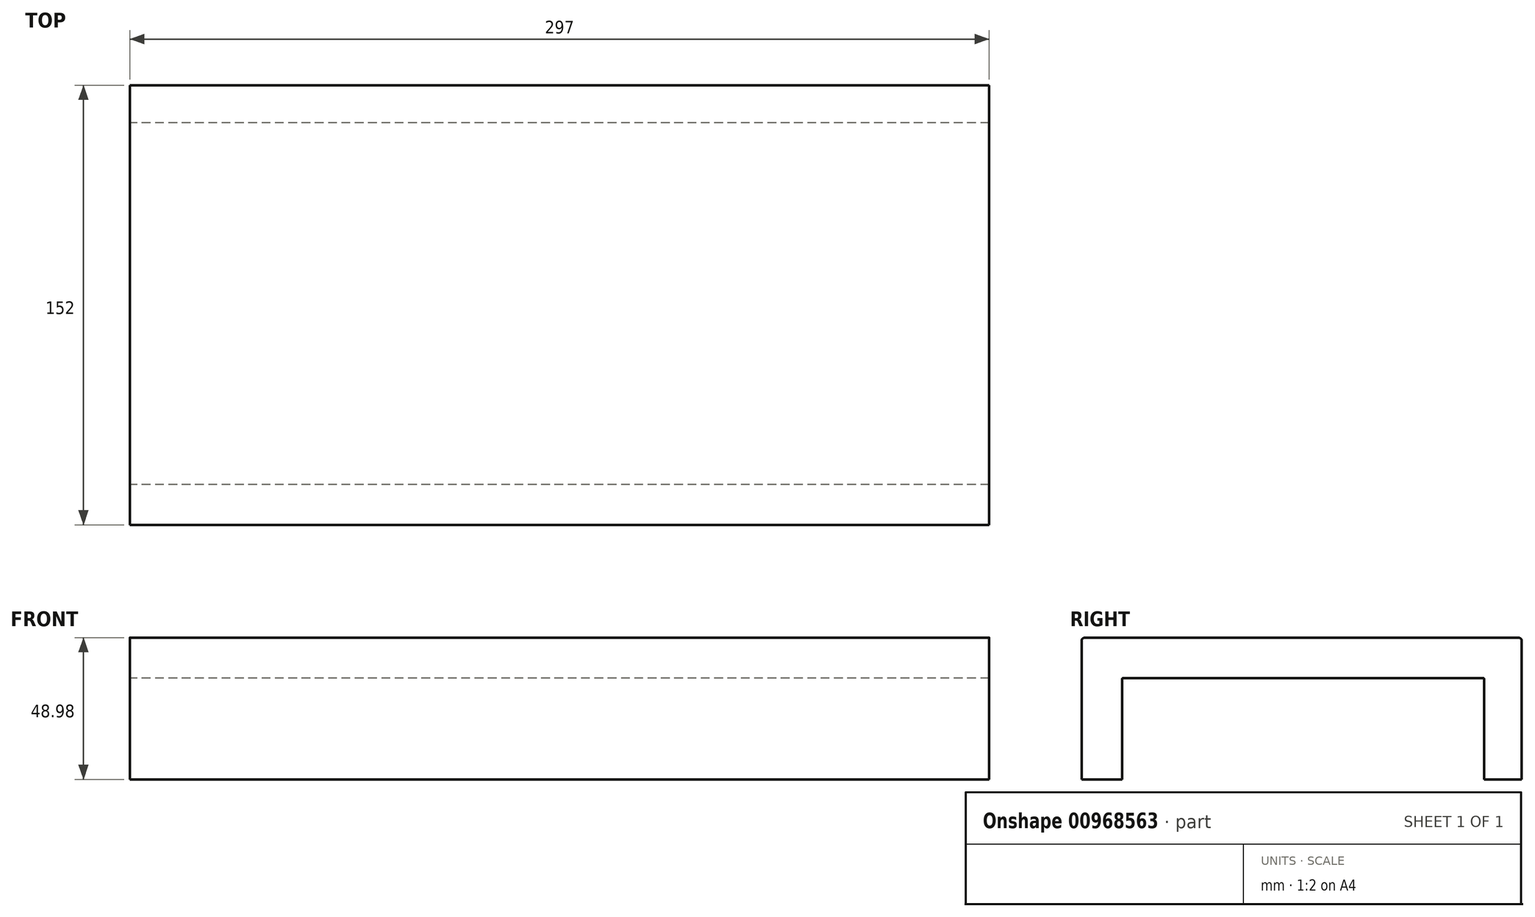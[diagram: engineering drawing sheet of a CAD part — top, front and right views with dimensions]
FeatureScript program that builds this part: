
annotation { "Feature Type Name" : "Feature", "Feature Type Description" : "" }
export const myFeature = defineFeature(function(context is Context, id is Id, definition is map)
    precondition{}
    {
        {
            var Q0;
            Q0=qCreatedBy(makeId("Right.planeOp"),FACE);
            var sketch = newSketch(context, id + "F0", { "sketchPlane" : qUnion([Q0])});
            skLineSegment(sketch, "E0", {"start": v(-48.76, 0) * mm, "end": v(-48.76, 47.98) * mm});
            skLineSegment(sketch, "E1", {"start": v(-47.76, 48.98) * mm, "end": v(102.24, 48.98) * mm});
            skLineSegment(sketch, "E2", {"start": v(103.24, 47.98) * mm, "end": v(103.24, 0) * mm});
            skLineSegment(sketch, "E3", {"start": v(103.24, 0) * mm, "end": v(90.24, 0) * mm});
            skLineSegment(sketch, "E4", {"start": v(90.24, 0) * mm, "end": v(90.24, 34.78) * mm});
            skLineSegment(sketch, "E5", {"start": v(90.04, 34.98) * mm, "end": v(-34.56, 34.98) * mm});
            skLineSegment(sketch, "E6", {"start": v(-34.76, 34.78) * mm, "end": v(-34.76, 0) * mm});
            skLineSegment(sketch, "E7", {"start": v(-34.76, 0) * mm, "end": v(-48.76, 0) * mm});
            skArc(sketch, "E8.filletArc", {"start": v(-47.76, 48.98) * mm, "mid": v(-48.47, 48.7) * mm, "end": v(-48.76, 47.98) * mm});
            skPoint(sketch, "E9.visualSharp", {"position": v(-34.76, 34.98) * mm});
            skArc(sketch, "E9.filletArc", {"start": v(-34.56, 34.98) * mm, "mid": v(-34.7, 34.93) * mm, "end": v(-34.76, 34.78) * mm});
            skPoint(sketch, "E10.visualSharp", {"position": v(90.24, 34.98) * mm});
            skArc(sketch, "E10.filletArc", {"start": v(90.24, 34.78) * mm, "mid": v(90.18, 34.93) * mm, "end": v(90.04, 34.98) * mm});
            skPoint(sketch, "E11.visualSharp", {"position": v(103.24, 48.98) * mm});
            skArc(sketch, "E11.filletArc", {"start": v(103.24, 47.98) * mm, "mid": v(102.95, 48.7) * mm, "end": v(102.24, 48.98) * mm});
            skSolve(sketch);
        }
        {
            var Q0;
            Q0 = qSketchRegion(id + "F0", true);
            extrude(context, id + "F1", {"entities" : qUnion([Q0]), "depth" : 297 * mm, "offsetDistance" : 25 * mm});
        }
    });
